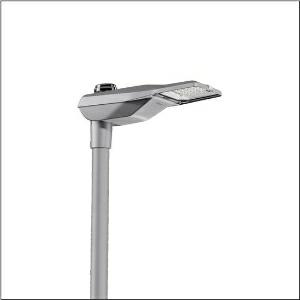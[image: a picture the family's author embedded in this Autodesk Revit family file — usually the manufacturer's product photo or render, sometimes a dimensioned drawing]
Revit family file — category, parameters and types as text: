
# Revit family: streetlight_sl_21_micro___st1_0a_5xe5d27n08db_a8cd
name_source: partatom
category: Lighting Fixtures
units: mm (PartAtom-declared; Revit-internal decimal feet)

## family parameters
Cut with Voids When Loaded = No
Host = Face
Light Source = No
Part Type = Normal
Room Calculation Point = No
Round Connector Dimension = Use Diameter
Shared = No

## types (1)
- --- (1 x LED, 4230 lm, 39.1 W, 2200K)
    Apparent Load = 39 VA
    CIE Flux Codes = 37 72 97 100 100
    Color Rendering = 70
    Color Temperature = 2200K
    Default Elevation = 1800 mm
    Description = Streetlight SL 21 micro, mast luminaire, primary light control with lens, of PMMA, primary optical cover: cover, of toughened safety glass, transparent, light distribution: ST1.0a, light emission: direct distribution, primary light characteristic: asymmetric, installation type: post-top, LED, 3G 1.5mm², High Power LED, rated luminous flux: 4.230lm, luminous efficacy: 108lm/W, light colour: 722, colour temperature: 2200K, control gear: NEMA (7pin), control: overheat protection, pre-setting: linear dimming characteristic, constant luminous flux control, time-dependent luminous flux control, flexible luminous flux parameterisation, mains connection: 230..240V, AC, 50/60Hz, connection cable pre-assembled, cable length: 6,5m, wiring characteristics: H07RN-F, start of lifetime: 39W, end of service life: 41W, reduction: 18W, luminaire housing, of diecast aluminium (EN AC-44300), powder-coated, SITECO metallic grey (DB 702S), corrosivity category C5 high according to DIN EN ISO 12944, multi-level sealing system, sealing non-destructively replaceable, inclination adjustable: 0°, 5°, 10°, 15°, length: 528mm, width: 235mm, height: 110mm, spigot size: 76/60mm (post-top), mounting height: 4..8m, protection rating (complete): IP66, insulation class (complete): insulation class I (protective earthing), certification: CE, ENEC, ENEC+, VDE, impact resistance: IK10, permissible operating ambient temperature for outdoor applications: -40..+50°C, standard-compliant lighting for roads and squares, packaging unit: 1 piece

Light Distribution: ST1.0a
    Height = 110 mm
    Lamp = 1 x LED
    Lamp Light Flux = 4230 lm
    Lamp Power = 39.1 W
    Lamp count = 1
    Length = 528 mm
    Luminous efficacy = 108 lm/W
    Manufacturer = Siteco
    ModVariant = No
    Model = 5XE5D27N08DB
    Number of Poles = 1
    OnlyDefault = Yes
    Power Factor = 1
    Product Name = Streetlight SL 21 micro | ST1.0a
    Product group = mast luminaire | pylon top
    ProductGroupID = 6100
    Protection Class = Protection class I
    Protection Degree = IP 66
    RLX_Detail_Level = 1
    RLX_Emergency_Light_Flux = 0 lm
    RLX_Emergency_Type = 0
    RLX_Emergency_Type_DB = No
    RlxData = <blob elided: 98817 chars, md5=270444ae>
    Socket = socket
    Standby Power = 0 W
    System Light Flux = 4230 lm
    System Power = 39 W
    Type Comments = factory setting: luminous flux: 100 % | dim-lin: 254 | 765 mA
    Type Image = l_1294375.jpg
    URL = http://relux.com
    VarID = @adj_136111
    Voltage = 0 V
    Weight = 0.00 kg
    Width = 235 mm

## geometry (parser evidence)
native form markers: Blend x4, Sweep x11
no freeform markers — native parametric forms only
